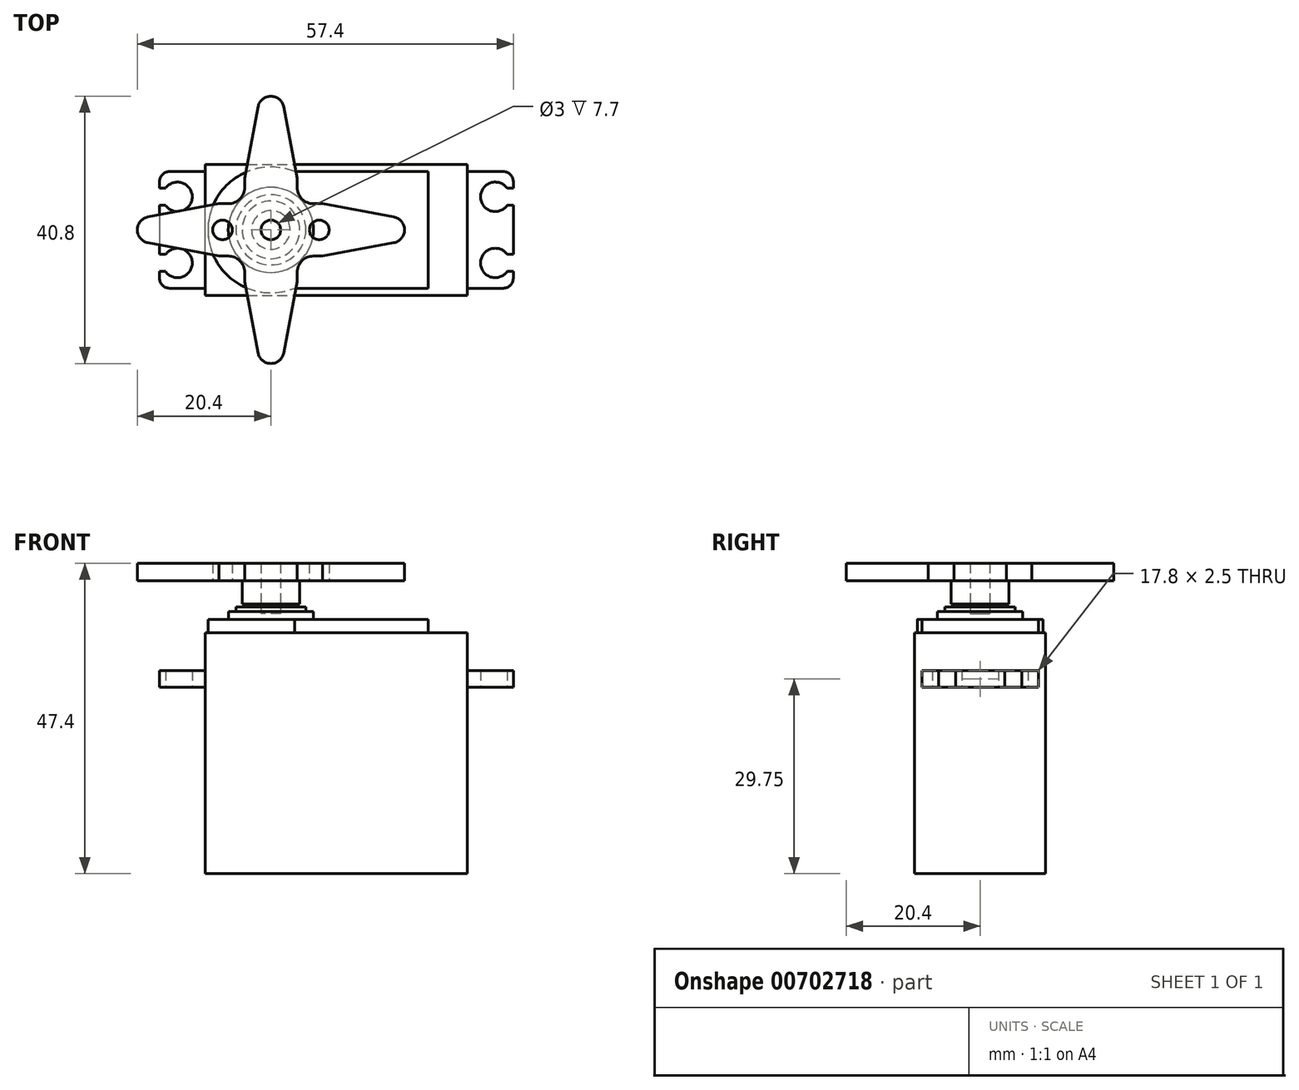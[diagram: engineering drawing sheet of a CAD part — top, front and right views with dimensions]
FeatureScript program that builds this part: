
annotation { "Feature Type Name" : "Feature", "Feature Type Description" : "" }
export const myFeature = defineFeature(function(context is Context, id is Id, definition is map)
    precondition{}
    {
        {
            var Q0;
            Q0=qCreatedBy(makeId("Top.planeOp"),FACE);
            var sketch = newSketch(context, id + "F0", { "sketchPlane" : qUnion([Q0])});
            skLineSegment(sketch, "E0.bottom", {"start": v(0, 0) * mm, "end": v(40, 0) * mm});
            skLineSegment(sketch, "E0.top", {"start": v(0, 20) * mm, "end": v(40, 20) * mm});
            skLineSegment(sketch, "E0.left", {"start": v(0, 0) * mm, "end": v(0, 20) * mm});
            skLineSegment(sketch, "E0.right", {"start": v(40, 0) * mm, "end": v(40, 20) * mm});
            skSolve(sketch);
        }
        {
            var Q0;
            Q0=makeQuery(id+"F0.imprint","IMPRINT",FACE,{"disambiguationData":[TD([[makeQuery(id+"F0.imprint","IMPRINT",EDGE,{"derivedFrom":sQuery(id+"F0.wireOp",EDGE,"E0.bottom")}),1.0]])]});
            extrude(context, id + "F1", {"entities" : qUnion([Q0]), "depth" : 28.5 * mm, "offsetDistance" : 25.4 * mm});
        }
        {
            var Q0;
            Q0=makeQuery(id+"F1.opExtrude","CAP_FACE",FACE,{"disambiguationData":[OSD([sQuery(id+"F0.wireOp",EDGE,"E0.bottom"),sQuery(id+"F0.wireOp",EDGE,"E0.top"),sQuery(id+"F0.wireOp",EDGE,"E0.left"),sQuery(id+"F0.wireOp",EDGE,"E0.right")])],"isStart":false});
            var sketch = newSketch(context, id + "F2", { "sketchPlane" : qUnion([Q0])});
            skLineSegment(sketch, "E1.bottom", {"start": v(0, 0) * mm, "end": v(40, 0) * mm});
            skLineSegment(sketch, "E1.top", {"start": v(0, 20) * mm, "end": v(40, 20) * mm});
            skLineSegment(sketch, "E1.left", {"start": v(0, 0) * mm, "end": v(0, 20) * mm});
            skLineSegment(sketch, "E1.right", {"start": v(40, 0) * mm, "end": v(40, 20) * mm});
            skLineSegment(sketch, "E2", {"start": v(40, 18.9) * mm, "end": v(47, 18.9) * mm});
            skLineSegment(sketch, "E3", {"start": v(-22.9, 10) * mm, "end": v(68.73, 10) * mm, "construction": true});
            skPoint(sketch, "E3.startSnap0", {"position": v(0, 10) * mm});
            skPoint(sketch, "E4", {"position": v(47, 10) * mm});
            skLineSegment(sketch, "E5", {"start": v(20, 20) * mm, "end": v(20, 0) * mm, "construction": true});
            skLineSegment(sketch, "E6", {"start": v(47, 18.9) * mm, "end": v(47, 16.35) * mm});
            skLineSegment(sketch, "E7", {"start": v(47, 16.35) * mm, "end": v(46.09, 16.35) * mm});
            skLineSegment(sketch, "E8", {"start": v(46.09, 13.75) * mm, "end": v(47, 13.75) * mm});
            skLineSegment(sketch, "E9", {"start": v(47, 13.75) * mm, "end": v(47, 10) * mm});
            skArc(sketch, "E10", {"start": v(46.09, 16.35) * mm, "mid": v(42, 15.05) * mm, "end": v(46.09, 13.75) * mm});
            skLineSegment(sketch, "E11.MirrorCS", {"start": v(46.09, 6.25) * mm, "end": v(47, 6.25) * mm});
            skLineSegment(sketch, "E12.MirrorCS", {"start": v(47, 3.65) * mm, "end": v(46.09, 3.65) * mm});
            skLineSegment(sketch, "E13.MirrorCS", {"start": v(40, 1.1) * mm, "end": v(47, 1.1) * mm});
            skLineSegment(sketch, "E14.MirrorCS", {"start": v(47, 1.1) * mm, "end": v(47, 3.65) * mm});
            skLineSegment(sketch, "E15.MirrorCS", {"start": v(47, 6.25) * mm, "end": v(47, 10) * mm});
            skArc(sketch, "E16.MirrorCS", {"start": v(46.09, 3.65) * mm, "mid": v(42, 4.95) * mm, "end": v(46.09, 6.25) * mm});
            skLineSegment(sketch, "E17.MirrorCS", {"start": v(20, 0) * mm, "end": v(20, 20) * mm, "construction": true});
            skLineSegment(sketch, "E18.MirrorCS", {"start": v(-7, 16.35) * mm, "end": v(-6.09, 16.35) * mm});
            skLineSegment(sketch, "E19.MirrorCS", {"start": v(-6.09, 13.75) * mm, "end": v(-7, 13.75) * mm});
            skLineSegment(sketch, "E20.MirrorCS", {"start": v(-6.09, 6.25) * mm, "end": v(-7, 6.25) * mm});
            skLineSegment(sketch, "E21.MirrorCS", {"start": v(-7, 3.65) * mm, "end": v(-6.09, 3.65) * mm});
            skLineSegment(sketch, "E22.MirrorCS", {"start": v(0, 18.9) * mm, "end": v(-7, 18.9) * mm});
            skLineSegment(sketch, "E23.MirrorCS", {"start": v(-7, 18.9) * mm, "end": v(-7, 16.35) * mm});
            skLineSegment(sketch, "E24.MirrorCS", {"start": v(-7, 13.75) * mm, "end": v(-7, 10) * mm});
            skPoint(sketch, "E25.MirrorP", {"position": v(-7, 10) * mm});
            skArc(sketch, "E26.MirrorCS", {"start": v(-6.09, 3.65) * mm, "mid": v(-2, 4.95) * mm, "end": v(-6.09, 6.25) * mm});
            skArc(sketch, "E27.MirrorCS", {"start": v(-6.09, 16.35) * mm, "mid": v(-2, 15.05) * mm, "end": v(-6.09, 13.75) * mm});
            skLineSegment(sketch, "E28.MirrorCS", {"start": v(-7, 6.25) * mm, "end": v(-7, 10) * mm});
            skLineSegment(sketch, "E29.MirrorCS", {"start": v(0, 1.1) * mm, "end": v(-7, 1.1) * mm});
            skLineSegment(sketch, "E30.MirrorCS", {"start": v(-7, 1.1) * mm, "end": v(-7, 3.65) * mm});
            skLineSegment(sketch, "E31", {"start": v(20, 20) * mm, "end": v(0, 20) * mm});
            skLineSegment(sketch, "E32", {"start": v(10, 20) * mm, "end": v(10, 0) * mm, "construction": true});
            skCircle(sketch, "E33", {"center": v(10, 10) * mm, "radius": 2.95 * mm});
            skCircle(sketch, "E34", {"center": v(10, 10) * mm, "radius": 5.35 * mm});
            skCircle(sketch, "E35", {"center": v(10, 10) * mm, "radius": 6.5 * mm});
            skArc(sketch, "E36", {"start": v(13.6, 18.9) * mm, "mid": v(0.4, 10) * mm, "end": v(13.6, 1.1) * mm});
            skLineSegment(sketch, "E37.0", {"start": v(13.6, 1.1) * mm, "end": v(34, 1.1) * mm});
            skLineSegment(sketch, "E38.0", {"start": v(34, 1.1) * mm, "end": v(34, 18.9) * mm});
            skLineSegment(sketch, "E39.MirrorCS", {"start": v(13.6, 18.9) * mm, "end": v(34, 18.9) * mm});
            skCircle(sketch, "E40", {"center": v(10, 10) * mm, "radius": 1.5 * mm});
            skSolve(sketch);
        }
        {
            var Q0;
            Q0=makeQuery(id+"F2.imprint","IMPRINT",FACE,{"disambiguationData":[TD([[makeQuery(id+"F2.imprint","IMPRINT",EDGE,{"derivedFrom":sQuery(id+"F2.wireOp",EDGE,"E18.MirrorCS")}),1.0]])]});
            var Q1;
            {var subQ1=sQuery(id+"F2.wireOp",EDGE,"E2");Q1=makeQuery(id+"F2.imprint","IMPRINT",FACE,{"disambiguationData":[TD([[makeQuery(id+"F2.imprint","IMPRINT",EDGE,{"derivedFrom":subQ1}),-1.0]])]});}
            extrude(context, id + "F3", {"entities" : qUnion([Q0, Q1]), "operationType" : NewBodyOperationType.ADD, "depth" : 2.5 * mm, "offsetDistance" : 25.4 * mm});
        }
        {
            var Q0;
            Q0=makeQuery(id+"F2.imprint","IMPRINT",FACE,{"disambiguationData":[TD([[makeQuery(id+"F2.imprint","IMPRINT",EDGE,{"derivedFrom":sQuery(id+"F2.wireOp",EDGE,"E33")}),1.0]])]});
            extrude(context, id + "F4", {"entities" : qUnion([Q0]), "operationType" : NewBodyOperationType.ADD, "depth" : 16.2 * mm, "offsetDistance" : 25.4 * mm});
        }
        {
            var Q0;
            Q0=makeQuery(id+"F2.imprint","IMPRINT",FACE,{"disambiguationData":[TD([[makeQuery(id+"F2.imprint","IMPRINT",EDGE,{"derivedFrom":sQuery(id+"F2.wireOp",EDGE,"E33")}),-1.0]])]});
            extrude(context, id + "F5", {"entities" : qUnion([Q0]), "operationType" : NewBodyOperationType.ADD, "depth" : 12.2 * mm, "offsetDistance" : 25.4 * mm});
        }
        {
            var Q0;
            Q0=makeQuery(id+"F2.imprint","IMPRINT",FACE,{"disambiguationData":[TD([[makeQuery(id+"F2.imprint","IMPRINT",EDGE,{"derivedFrom":sQuery(id+"F2.wireOp",EDGE,"E34")}),-1.0]])]});
            extrude(context, id + "F6", {"entities" : qUnion([Q0]), "operationType" : NewBodyOperationType.ADD, "depth" : 11.5 * mm, "offsetDistance" : 25.4 * mm});
        }
        {
            var Q0;
            Q0=makeQuery(id+"F2.imprint","IMPRINT",FACE,{"disambiguationData":[TD([[makeQuery(id+"F2.imprint","IMPRINT",EDGE,{"derivedFrom":sQuery(id+"F2.wireOp",EDGE,"E35")}),-1.0]])]});
            extrude(context, id + "F7", {"entities" : qUnion([Q0]), "operationType" : NewBodyOperationType.ADD, "depth" : 10.3 * mm, "offsetDistance" : 25.4 * mm});
        }
        {
            var Q0;
            {var subQ5=sQuery(id+"F2.wireOp",EDGE,"E1.bottom");Q0=makeQuery(id+"F2.imprint","IMPRINT",FACE,{"disambiguationData":[TD([[makeQuery(id+"F2.imprint","IMPRINT",EDGE,{"derivedFrom":subQ5}),1.0]])]});}
            extrude(context, id + "F8", {"entities" : qUnion([Q0]), "operationType" : NewBodyOperationType.ADD, "depth" : 8.3 * mm, "offsetDistance" : 25.4 * mm});
        }
        {
            var Q0;
            Q0=makeQuery(id+"F2.imprint","IMPRINT",FACE,{"disambiguationData":[TD([[makeQuery(id+"F2.imprint","IMPRINT",EDGE,{"derivedFrom":sQuery(id+"F2.wireOp",EDGE,"E40")}),1.0]])]});
            extrude(context, id + "F9", {"entities" : qUnion([Q0]), "operationType" : NewBodyOperationType.ADD, "depth" : 11.2 * mm, "offsetDistance" : 25.4 * mm});
        }
        {
            var Q0;
            Q0=makeQuery(id+"F3.opExtrude","SWEPT_EDGE",EDGE,{"disambiguationData":[OSD([sQuery(id+"F2.wireOp",EDGE,"E29.MirrorCS"),sQuery(id+"F2.wireOp",EDGE,"E30.MirrorCS")])]});
            var Q1;
            Q1=makeQuery(id+"F3.opExtrude","SWEPT_EDGE",EDGE,{"disambiguationData":[OSD([sQuery(id+"F2.wireOp",EDGE,"E22.MirrorCS"),sQuery(id+"F2.wireOp",EDGE,"E23.MirrorCS")])]});
            var Q2;
            Q2=makeQuery(id+"F3.opExtrude","SWEPT_EDGE",EDGE,{"disambiguationData":[OSD([sQuery(id+"F2.wireOp",EDGE,"E13.MirrorCS"),sQuery(id+"F2.wireOp",EDGE,"E14.MirrorCS")])]});
            var Q3;
            Q3=makeQuery(id+"F3.opExtrude","SWEPT_EDGE",EDGE,{"disambiguationData":[OSD([sQuery(id+"F2.wireOp",EDGE,"E2"),sQuery(id+"F2.wireOp",EDGE,"E6")])]});
            fillet(context, id + "F10", {"entities" : qUnion([Q0, Q1, Q2, Q3]), "radius" : 1.5 * mm, "tangentPropagation" : true, "allowEdgeOverflow" : false});
        }
        {
            var Q0;
            Q0=makeQuery(id+"F4.opExtrude","CAP_FACE",FACE,{"disambiguationData":[OSD([sQuery(id+"F2.wireOp",EDGE,"E33"),sQuery(id+"F2.wireOp",EDGE,"E40")])],"isStart":false});
            var sketch = newSketch(context, id + "F11", { "sketchPlane" : qUnion([Q0])});
            skCircle(sketch, "E41", {"center": v(10, 10) * mm, "radius": 4.4 * mm});
            skCircle(sketch, "E42", {"center": v(10, 10) * mm, "radius": 2.95 * mm});
            skLineSegment(sketch, "E43.0", {"start": v(16.5, 14) * mm, "end": v(17.9, 14) * mm});
            skLineSegment(sketch, "E44", {"start": v(17.9, 14) * mm, "end": v(28.77, 11.97) * mm});
            skLineSegment(sketch, "E45.MirrorCS", {"start": v(17.9, 6) * mm, "end": v(28.77, 8.03) * mm});
            skLineSegment(sketch, "E46.MirrorCS", {"start": v(16.5, 6) * mm, "end": v(17.9, 6) * mm});
            skArc(sketch, "E47", {"start": v(28.77, 8.03) * mm, "mid": v(30.4, 10) * mm, "end": v(28.77, 11.97) * mm});
            skLineSegment(sketch, "E48.1.0", {"start": v(6, 16.5) * mm, "end": v(6, 17.9) * mm});
            skLineSegment(sketch, "E48.1.1", {"start": v(6, 17.9) * mm, "end": v(8.03, 28.77) * mm});
            skArc(sketch, "E48.1.2", {"start": v(11.97, 28.77) * mm, "mid": v(10, 30.4) * mm, "end": v(8.03, 28.77) * mm});
            skLineSegment(sketch, "E48.1.3", {"start": v(14, 17.9) * mm, "end": v(11.97, 28.77) * mm});
            skLineSegment(sketch, "E48.1.4", {"start": v(14, 16.5) * mm, "end": v(14, 17.9) * mm});
            skLineSegment(sketch, "E48.2.0", {"start": v(3.5, 6) * mm, "end": v(2.1, 6) * mm});
            skLineSegment(sketch, "E48.2.1", {"start": v(2.1, 6) * mm, "end": v(-8.77, 8.03) * mm});
            skArc(sketch, "E48.2.2", {"start": v(-8.77, 11.97) * mm, "mid": v(-10.4, 10) * mm, "end": v(-8.77, 8.03) * mm});
            skLineSegment(sketch, "E48.2.3", {"start": v(2.1, 14) * mm, "end": v(-8.77, 11.97) * mm});
            skLineSegment(sketch, "E48.2.4", {"start": v(3.5, 14) * mm, "end": v(2.1, 14) * mm});
            skLineSegment(sketch, "E48.3.0", {"start": v(14, 3.5) * mm, "end": v(14, 2.1) * mm});
            skLineSegment(sketch, "E48.3.1", {"start": v(14, 2.1) * mm, "end": v(11.97, -8.77) * mm});
            skArc(sketch, "E48.3.2", {"start": v(8.03, -8.77) * mm, "mid": v(10, -10.4) * mm, "end": v(11.97, -8.77) * mm});
            skLineSegment(sketch, "E48.3.3", {"start": v(6, 2.1) * mm, "end": v(8.03, -8.77) * mm});
            skLineSegment(sketch, "E48.3.4", {"start": v(6, 3.5) * mm, "end": v(6, 2.1) * mm});
            skPoint(sketch, "E49.visualSharp", {"position": v(14, 14) * mm});
            skArc(sketch, "E49.filletArc", {"start": v(14, 16.5) * mm, "mid": v(14.73, 14.73) * mm, "end": v(16.5, 14) * mm});
            skPoint(sketch, "E50.visualSharp", {"position": v(14, 6) * mm});
            skArc(sketch, "E50.filletArc", {"start": v(16.5, 6) * mm, "mid": v(14.73, 5.27) * mm, "end": v(14, 3.5) * mm});
            skPoint(sketch, "E51.visualSharp", {"position": v(6, 6) * mm});
            skArc(sketch, "E51.filletArc", {"start": v(6, 3.5) * mm, "mid": v(5.27, 5.27) * mm, "end": v(3.5, 6) * mm});
            skPoint(sketch, "E52.visualSharp", {"position": v(6, 14) * mm});
            skArc(sketch, "E52.filletArc", {"start": v(3.5, 14) * mm, "mid": v(5.27, 14.73) * mm, "end": v(6, 16.5) * mm});
            skCircle(sketch, "E53", {"center": v(17.38, 10) * mm, "radius": 1.5 * mm});
            skCircle(sketch, "E54.MirrorC", {"center": v(2.62, 10) * mm, "radius": 1.5 * mm});
            skSolve(sketch);
        }
        {
            var Q0;
            Q0=makeQuery(id+"F11.imprint","IMPRINT",FACE,{"disambiguationData":[TD([[makeQuery(id+"F11.imprint","IMPRINT",EDGE,{"derivedFrom":sQuery(id+"F11.wireOp",EDGE,"E41")}),1.0]])]});
            extrude(context, id + "F12", {"entities" : qUnion([Q0]), "oppositeDirection" : true, "depth" : 3.5 * mm, "offsetDistance" : 25.4 * mm});
        }
        {
            var Q0;
            Q0=makeQuery(id+"F11.imprint","IMPRINT",FACE,{"disambiguationData":[TD([[makeQuery(id+"F11.imprint","IMPRINT",EDGE,{"derivedFrom":sQuery(id+"F11.wireOp",EDGE,"E41")}),-1.0]])]});
            var Q1;
            Q1=makeQuery(id+"F11.imprint","IMPRINT",FACE,{"disambiguationData":[TD([[makeQuery(id+"F11.imprint","IMPRINT",EDGE,{"derivedFrom":sQuery(id+"F11.wireOp",EDGE,"E42")}),1.0]])]});
            var Q2;
            Q2=makeQuery(id+"F11.imprint","IMPRINT",FACE,{"disambiguationData":[TD([[makeQuery(id+"F11.imprint","IMPRINT",EDGE,{"derivedFrom":sQuery(id+"F11.wireOp",EDGE,"E41")}),1.0]])]});
            extrude(context, id + "F13", {"entities" : qUnion([Q0, Q1, Q2]), "operationType" : NewBodyOperationType.ADD, "depth" : 2.7 * mm, "offsetDistance" : 25.4 * mm});
        }
    });
